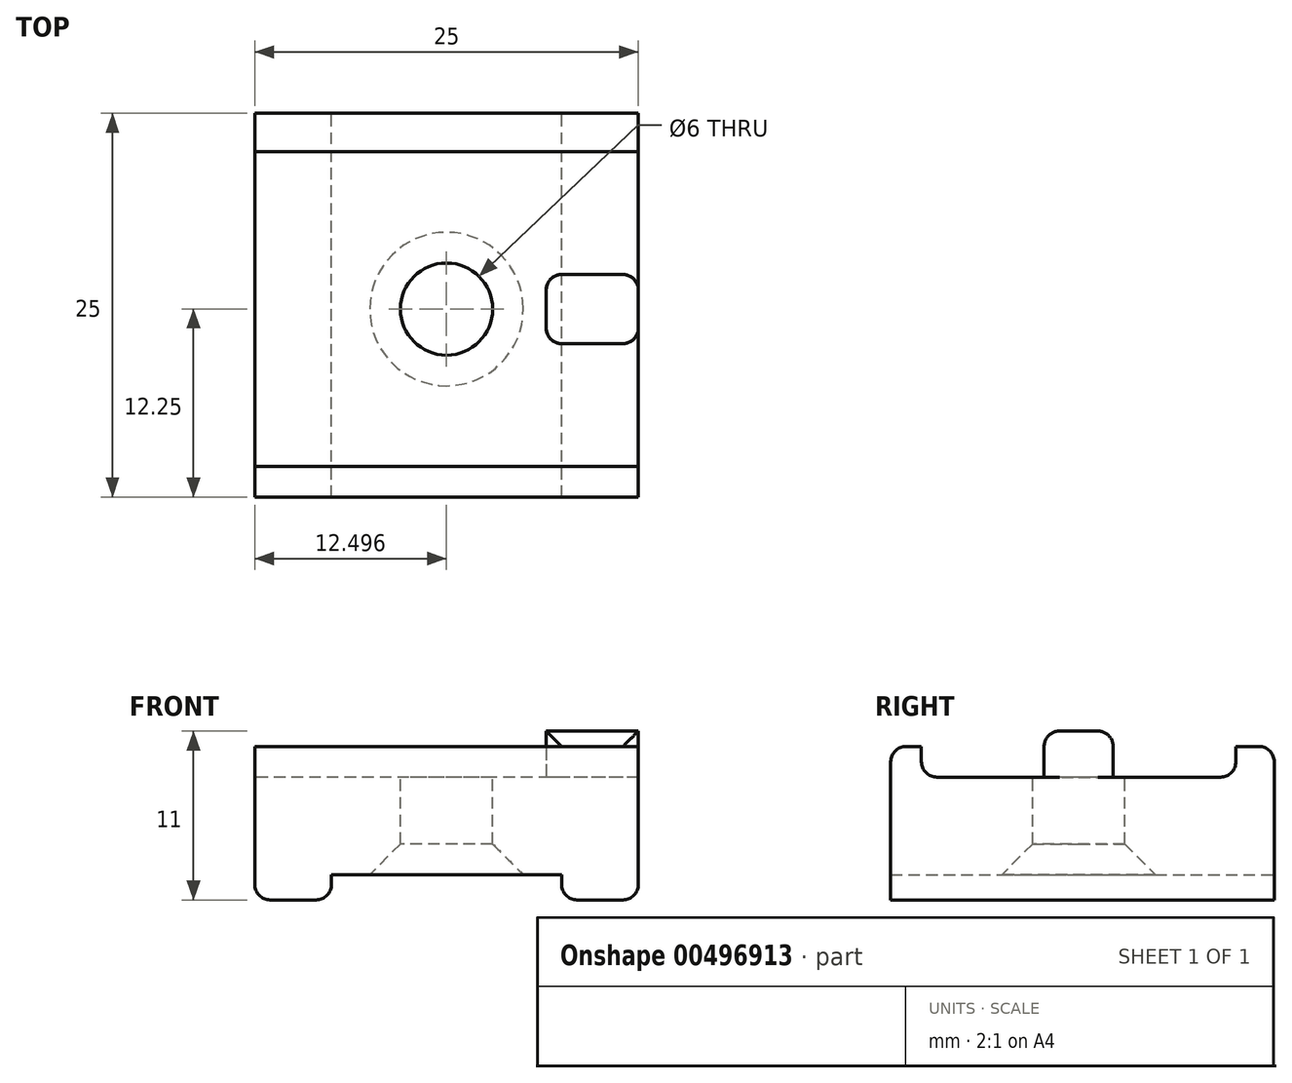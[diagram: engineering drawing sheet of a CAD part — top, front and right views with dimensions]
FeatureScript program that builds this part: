
annotation { "Feature Type Name" : "Feature", "Feature Type Description" : "" }
export const myFeature = defineFeature(function(context is Context, id is Id, definition is map)
    precondition{}
    {
        {
            var Q0;
            Q0=qCreatedBy(makeId("Front.planeOp"),FACE);
            var sketch = newSketch(context, id + "F0", { "sketchPlane" : qUnion([Q0])});
            skLineSegment(sketch, "E0.bottom", {"start": v(-10.16, 10) * mm, "end": v(14.84, 10) * mm});
            skLineSegment(sketch, "E0.top", {"start": v(-10.16, 0) * mm, "end": v(-5.16, 0) * mm});
            skLineSegment(sketch, "E0.left", {"start": v(-10.16, 10) * mm, "end": v(-10.16, 0) * mm});
            skLineSegment(sketch, "E0.right", {"start": v(14.84, 10) * mm, "end": v(14.84, 0) * mm});
            skLineSegment(sketch, "E1.top", {"start": v(-5.16, 1.65) * mm, "end": v(9.84, 1.65) * mm});
            skLineSegment(sketch, "E1.left", {"start": v(-5.16, 0) * mm, "end": v(-5.16, 1.65) * mm});
            skLineSegment(sketch, "E1.right", {"start": v(9.84, 0) * mm, "end": v(9.84, 1.65) * mm});
            skLineSegment(sketch, "E2.trimOffspring", {"start": v(9.84, 0) * mm, "end": v(14.84, 0) * mm});
            skSolve(sketch);
        }
        {
            var Q0;
            Q0=makeQuery(id+"F0.imprint","IMPRINT",FACE,{"disambiguationData":[TD([[makeQuery(id+"F0.imprint","IMPRINT",EDGE,{"derivedFrom":sQuery(id+"F0.wireOp",EDGE,"E0.bottom")}),-1.0]])]});
            extrude(context, id + "F1", {"entities" : qUnion([Q0]), "depth" : 25 * mm});
        }
        {
            var Q0;
            Q0=makeQuery(id+"F1.opExtrude","SWEPT_FACE",FACE,{"disambiguationData":[OSD([sQuery(id+"F0.wireOp",EDGE,"E0.left")])]});
            var sketch = newSketch(context, id + "F2", { "sketchPlane" : qUnion([Q0])});
            skLineSegment(sketch, "E3.bottom", {"start": v(2.5, 10) * mm, "end": v(23, 10) * mm});
            skLineSegment(sketch, "E3.top", {"start": v(2.5, 8) * mm, "end": v(23, 8) * mm});
            skLineSegment(sketch, "E3.left", {"start": v(2.5, 10) * mm, "end": v(2.5, 8) * mm});
            skLineSegment(sketch, "E3.right", {"start": v(23, 10) * mm, "end": v(23, 8) * mm});
            skSolve(sketch);
        }
        {
            var Q0;
            Q0=makeQuery(id+"F2.imprint","IMPRINT",FACE,{"disambiguationData":[TD([[makeQuery(id+"F2.imprint","IMPRINT",EDGE,{"derivedFrom":sQuery(id+"F2.wireOp",EDGE,"E3.bottom")}),1.0]])]});
            extrude(context, id + "F3", {"entities" : qUnion([Q0]), "operationType" : NewBodyOperationType.REMOVE, "oppositeDirection" : true, "depth" : 25 * mm});
        }
        {
            var Q0;
            Q0=makeQuery(id+"F3.boolean.opBoolean","COPY",FACE,{"derivedFrom":makeQuery(id+"F3.opExtrude","SWEPT_FACE",FACE,{"disambiguationData":[OSD([sQuery(id+"F2.wireOp",EDGE,"E3.top")])]})});
            var sketch = newSketch(context, id + "F4", { "sketchPlane" : qUnion([Q0])});
            skLineSegment(sketch, "E4.bottom", {"start": v(14.84, -10.5) * mm, "end": v(8.84, -10.5) * mm});
            skLineSegment(sketch, "E4.top", {"start": v(14.84, -15) * mm, "end": v(8.84, -15) * mm});
            skLineSegment(sketch, "E4.left", {"start": v(14.84, -10.5) * mm, "end": v(14.84, -15) * mm});
            skLineSegment(sketch, "E4.right", {"start": v(8.84, -10.5) * mm, "end": v(8.84, -15) * mm});
            skCircle(sketch, "E5", {"center": v(2.34, -12.75) * mm, "radius": 3 * mm});
            skPoint(sketch, "E5.centerSnap0", {"position": v(8.84, -12.75) * mm});
            skSolve(sketch);
        }
        {
            var Q0;
            Q0=makeQuery(id+"F4.imprint","IMPRINT",FACE,{"disambiguationData":[TD([[makeQuery(id+"F4.imprint","IMPRINT",EDGE,{"derivedFrom":sQuery(id+"F4.wireOp",EDGE,"E5")}),1.0]])]});
            extrude(context, id + "F5", {"entities" : qUnion([Q0]), "operationType" : NewBodyOperationType.REMOVE, "oppositeDirection" : true, "depth" : 25 * mm});
        }
        {
            var Q0;
            Q0=makeQuery(id+"F4.imprint","IMPRINT",FACE,{"disambiguationData":[TD([[makeQuery(id+"F4.imprint","IMPRINT",EDGE,{"derivedFrom":sQuery(id+"F4.wireOp",EDGE,"E4.bottom")}),1.0]])]});
            extrude(context, id + "F6", {"entities" : qUnion([Q0]), "operationType" : NewBodyOperationType.ADD, "depth" : 3 * mm});
        }
        {
            var Q0;
            Q0=makeQuery(id+"F6.opExtrude","CAP_EDGE",EDGE,{"disambiguationData":[OSD([sQuery(id+"F4.wireOp",EDGE,"E4.bottom")])],"isStart":false});
            var Q1;
            Q1=makeQuery(id+"F6.opExtrude","CAP_EDGE",EDGE,{"disambiguationData":[OSD([sQuery(id+"F4.wireOp",EDGE,"E4.top")])],"isStart":false});
            var Q2;
            Q2=makeQuery(id+"F6.opExtrude","SWEPT_EDGE",EDGE,{"disambiguationData":[OSD([sQuery(id+"F4.wireOp",EDGE,"E4.bottom"),sQuery(id+"F4.wireOp",EDGE,"E4.right")])]});
            var Q3;
            Q3=makeQuery(id+"F6.opExtrude","SWEPT_EDGE",EDGE,{"disambiguationData":[OSD([sQuery(id+"F4.wireOp",EDGE,"E4.top"),sQuery(id+"F4.wireOp",EDGE,"E4.right")])]});
            var Q4;
            Q4=makeQuery(id+"F6.opExtrude","SWEPT_EDGE",EDGE,{"disambiguationData":[OSD([sQuery(id+"F0.wireOp",EDGE,"E0.right"),sQuery(id+"F2.wireOp",EDGE,"E3.top"),sQuery(id+"F4.wireOp",EDGE,"E4.bottom"),sQuery(id+"F4.wireOp",EDGE,"E4.left")])]});
            var Q5;
            Q5=makeQuery(id+"F6.opExtrude","SWEPT_EDGE",EDGE,{"disambiguationData":[OSD([sQuery(id+"F0.wireOp",EDGE,"E0.right"),sQuery(id+"F2.wireOp",EDGE,"E3.top"),sQuery(id+"F4.wireOp",EDGE,"E4.top"),sQuery(id+"F4.wireOp",EDGE,"E4.left")])]});
            fillet(context, id + "F7", {"entities" : qUnion([Q0, Q1, Q2, Q3, Q4, Q5]), "radius" : 1 * mm, "tangentPropagation" : true, "allowEdgeOverflow" : false});
        }
        {
            var Q0;
            Q0=makeQuery(id+"F3.boolean.opBoolean","COPY",EDGE,{"derivedFrom":makeQuery(id+"F3.opExtrude","SWEPT_EDGE",EDGE,{"disambiguationData":[OSD([sQuery(id+"F2.wireOp",EDGE,"E3.top"),sQuery(id+"F2.wireOp",EDGE,"E3.right")])]})});
            var Q1;
            Q1=makeQuery(id+"F3.boolean.opBoolean","COPY",EDGE,{"derivedFrom":makeQuery(id+"F3.opExtrude","SWEPT_EDGE",EDGE,{"disambiguationData":[OSD([sQuery(id+"F2.wireOp",EDGE,"E3.top"),sQuery(id+"F2.wireOp",EDGE,"E3.left")])]})});
            var Q2;
            Q2=makeQuery(id+"F1.opExtrude","CAP_EDGE",EDGE,{"disambiguationData":[OSD([sQuery(id+"F0.wireOp",EDGE,"E0.bottom")])],"isStart":false});
            var Q3;
            Q3=makeQuery(id+"F1.opExtrude","CAP_EDGE",EDGE,{"disambiguationData":[OSD([sQuery(id+"F0.wireOp",EDGE,"E0.bottom")])],"isStart":true});
            var Q4;
            Q4=makeQuery(id+"F1.opExtrude","SWEPT_EDGE",EDGE,{"disambiguationData":[OSD([sQuery(id+"F0.wireOp",EDGE,"E0.top"),sQuery(id+"F0.wireOp",EDGE,"E0.left")])]});
            var Q5;
            {var subQ0=sQuery(id+"F0.wireOp",EDGE,"E1.left");var subQ1=sQuery(id+"F0.wireOp",EDGE,"E0.top");Q5=makeQuery(id+"F5.boolean.opBoolean","SPLIT",EDGE,{"disambiguationData":[TD([makeQuery(id+"F1.opExtrude","CAP_FACE",FACE,{"disambiguationData":[OSD([sQuery(id+"F0.wireOp",EDGE,"E0.bottom"),subQ1,sQuery(id+"F0.wireOp",EDGE,"E0.left"),sQuery(id+"F0.wireOp",EDGE,"E0.right"),sQuery(id+"F0.wireOp",EDGE,"E1.top"),subQ0,sQuery(id+"F0.wireOp",EDGE,"E1.right"),sQuery(id+"F0.wireOp",EDGE,"E2.trimOffspring")])],"isStart":true})])],"derivedFrom":makeQuery(id+"F1.opExtrude","SWEPT_EDGE",EDGE,{"disambiguationData":[OSD([subQ1,subQ0])]})});}
            var Q6;
            Q6=makeQuery(id+"F1.opExtrude","SWEPT_EDGE",EDGE,{"disambiguationData":[OSD([sQuery(id+"F0.wireOp",EDGE,"E1.right"),sQuery(id+"F0.wireOp",EDGE,"E2.trimOffspring")])]});
            var Q7;
            Q7=makeQuery(id+"F1.opExtrude","SWEPT_EDGE",EDGE,{"disambiguationData":[OSD([sQuery(id+"F0.wireOp",EDGE,"E0.right"),sQuery(id+"F0.wireOp",EDGE,"E2.trimOffspring")])]});
            fillet(context, id + "F8", {"entities" : qUnion([Q0, Q1, Q2, Q3, Q4, Q5, Q6, Q7]), "radius" : 1 * mm, "tangentPropagation" : true, "allowEdgeOverflow" : false});
        }
        {
            var Q0;
            Q0=makeQuery(id+"F5.boolean.opBoolean","INTERSECT",EDGE,{"derivedFrom":[makeQuery(id+"F1.opExtrude","SWEPT_FACE",FACE,{"disambiguationData":[OSD([sQuery(id+"F0.wireOp",EDGE,"E1.top")])]}),makeQuery(id+"F5.opExtrude","SWEPT_FACE",FACE,{"disambiguationData":[OSD([sQuery(id+"F4.wireOp",EDGE,"E5")])]})]});
            chamfer(context, id + "F9", {"entities" : qUnion([Q0]), "width" : 2 * mm, "tangentPropagation" : true});
        }
    });
